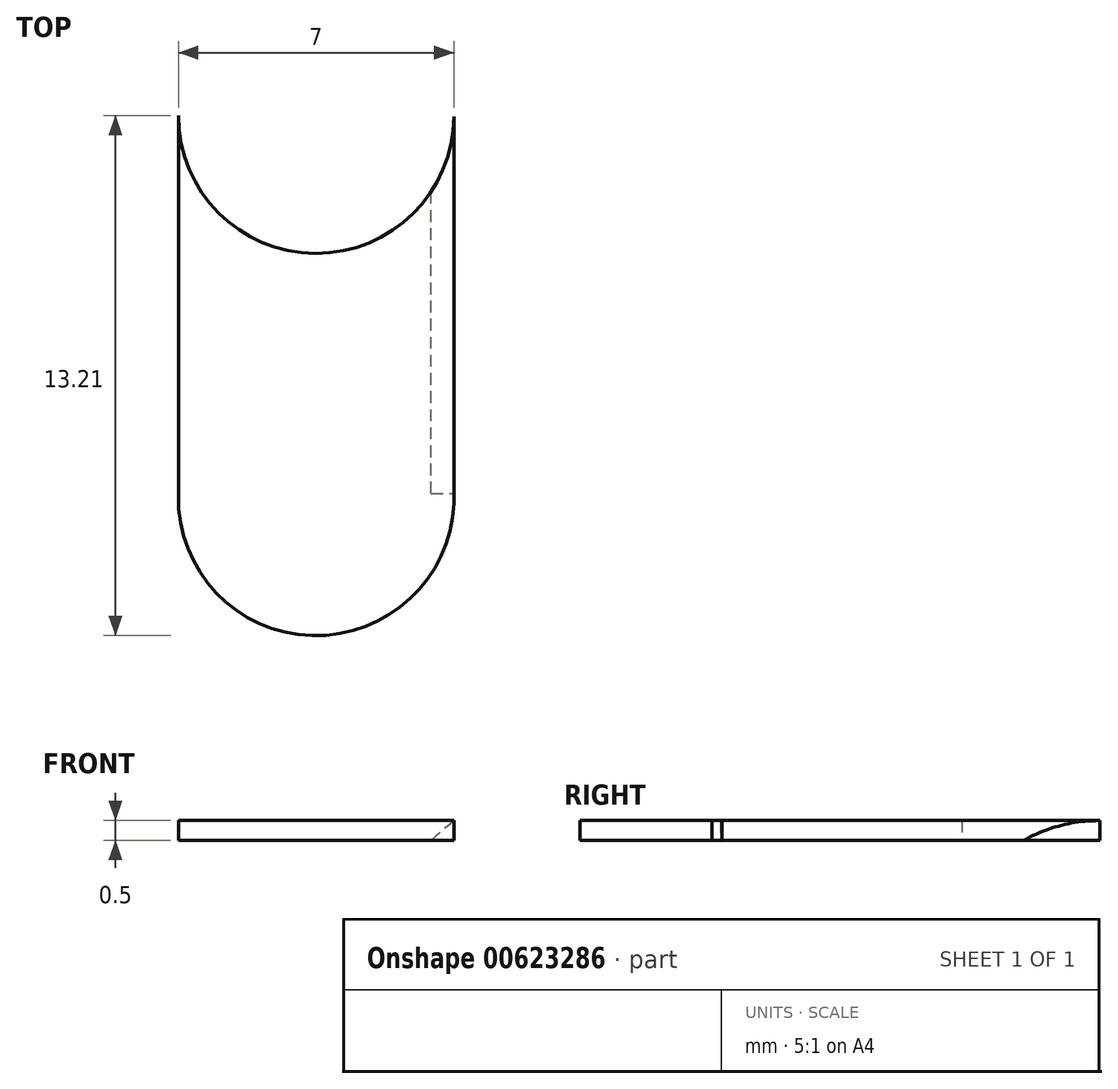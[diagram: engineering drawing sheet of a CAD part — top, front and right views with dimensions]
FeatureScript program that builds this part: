
annotation { "Feature Type Name" : "Feature", "Feature Type Description" : "" }
export const myFeature = defineFeature(function(context is Context, id is Id, definition is map)
    precondition{}
    {
        {
            var Q0;
            Q0=qCreatedBy(makeId("Top.planeOp"),FACE);
            var sketch = newSketch(context, id + "F0", { "sketchPlane" : qUnion([Q0])});
            skLineSegment(sketch, "E0", {"start": v(-3.5, -9.64) * mm, "end": v(-3.5, -9.64) * mm});
            skLineSegment(sketch, "E1", {"start": v(3.5, 0) * mm, "end": v(3.5, -9.85) * mm});
            skArc(sketch, "E2", {"start": v(-3.5, 0) * mm, "mid": v(0, -3.5) * mm, "end": v(3.5, 0) * mm});
            skArc(sketch, "E3", {"start": v(3.5, 0) * mm, "mid": v(0, 3.5) * mm, "end": v(-3.5, 0) * mm});
            skLineSegment(sketch, "E4", {"start": v(-3.5, -9.64) * mm, "end": v(-3.5, 0) * mm});
            skArc(sketch, "E5", {"start": v(3.5, -9.85) * mm, "mid": v(0.1, -6.21) * mm, "end": v(-3.5, -9.64) * mm});
            skArc(sketch, "E6", {"start": v(-3.5, -9.64) * mm, "mid": v(-0.1, -13.21) * mm, "end": v(3.5, -9.85) * mm});
            skSolve(sketch);
        }
        {
            var Q0;
            {var subQ0=sQuery(id+"F0.wireOp",EDGE,"E6");Q0=makeQuery(id+"F0.imprint","IMPRINT",FACE,{"disambiguationData":[TD([[makeQuery(id+"F0.imprint","IMPRINT",EDGE,{"derivedFrom":subQ0}),1.0]])]});}
            var Q1;
            {var subQ0=sQuery(id+"F0.wireOp",EDGE,"E2");Q1=makeQuery(id+"F0.imprint","IMPRINT",FACE,{"disambiguationData":[TD([[makeQuery(id+"F0.imprint","IMPRINT",EDGE,{"derivedFrom":subQ0}),-1.0]])]});}
            var Q2;
            Q2=sQuery(id+"F0.wireOp",EDGE,"E4");
            var Q3;
            Q3=sQuery(id+"F0.wireOp",EDGE,"E1");
            var Q4;
            Q4=sQuery(id+"F0.wireOp",EDGE,"E6");
            var Q5;
            Q5=sQuery(id+"F0.wireOp",EDGE,"E2");
            extrude(context, id + "F1", {"entities" : qUnion([Q0, Q1]), "surfaceEntities" : qUnion([Q2, Q3, Q4, Q5]), "depth" : 0.5 * mm, "offsetDistance" : 25 * mm});
        }
        {
            var Q0;
            Q0=qCreatedBy(makeId("Front.planeOp"),FACE);
            var sketch = newSketch(context, id + "F2", { "sketchPlane" : qUnion([Q0])});
            skLineSegment(sketch, "E7", {"start": v(3.52, 0.52) * mm, "end": v(2.92, 0) * mm});
            skLineSegment(sketch, "E8", {"start": v(2.92, 0) * mm, "end": v(3.52, 0) * mm});
            skLineSegment(sketch, "E9", {"start": v(3.52, 0) * mm, "end": v(3.52, 0.52) * mm});
            skSolve(sketch);
        }
        {
            var Q0;
            Q0=makeQuery(id+"FPdYwwzAGo0SVIA_1.1.F2.imprint","IMPRINT",FACE,{"disambiguationData":[TD([[makeQuery(id+"FPdYwwzAGo0SVIA_1.1.F2.imprint","IMPRINT",EDGE,{"derivedFrom":sQuery(id+"FPdYwwzAGo0SVIA_1.1.F2.wireOp",EDGE,"E7")}),1.0]])]});
            var Q1;
            Q1=makeQuery(id+"F2.imprint","IMPRINT",FACE,{"disambiguationData":[TD([[makeQuery(id+"F2.imprint","IMPRINT",EDGE,{"derivedFrom":sQuery(id+"F2.wireOp",EDGE,"E7")}),1.0]])]});
            var Q2;
            Q2=sQuery(id+"FPdYwwzAGo0SVIA_1.1.F2.wireOp",EDGE,"E7");
            var Q3;
            Q3=sQuery(id+"FPdYwwzAGo0SVIA_1.1.F2.wireOp",EDGE,"E8");
            var Q4;
            Q4=sQuery(id+"FPdYwwzAGo0SVIA_1.1.F2.wireOp",EDGE,"E9");
            var Q5;
            Q5=sQuery(id+"F2.wireOp",EDGE,"E8");
            var Q6;
            Q6=sQuery(id+"F2.wireOp",EDGE,"E9");
            var Q7;
            Q7=sQuery(id+"F2.wireOp",EDGE,"E7");
            extrude(context, id + "F3", {"entities" : qUnion([Q0, Q1]), "operationType" : NewBodyOperationType.REMOVE, "surfaceEntities" : qUnion([Q2, Q3, Q4, Q5, Q6, Q7]), "depth" : 9.6 * mm, "offsetDistance" : 25 * mm});
        }
    });
